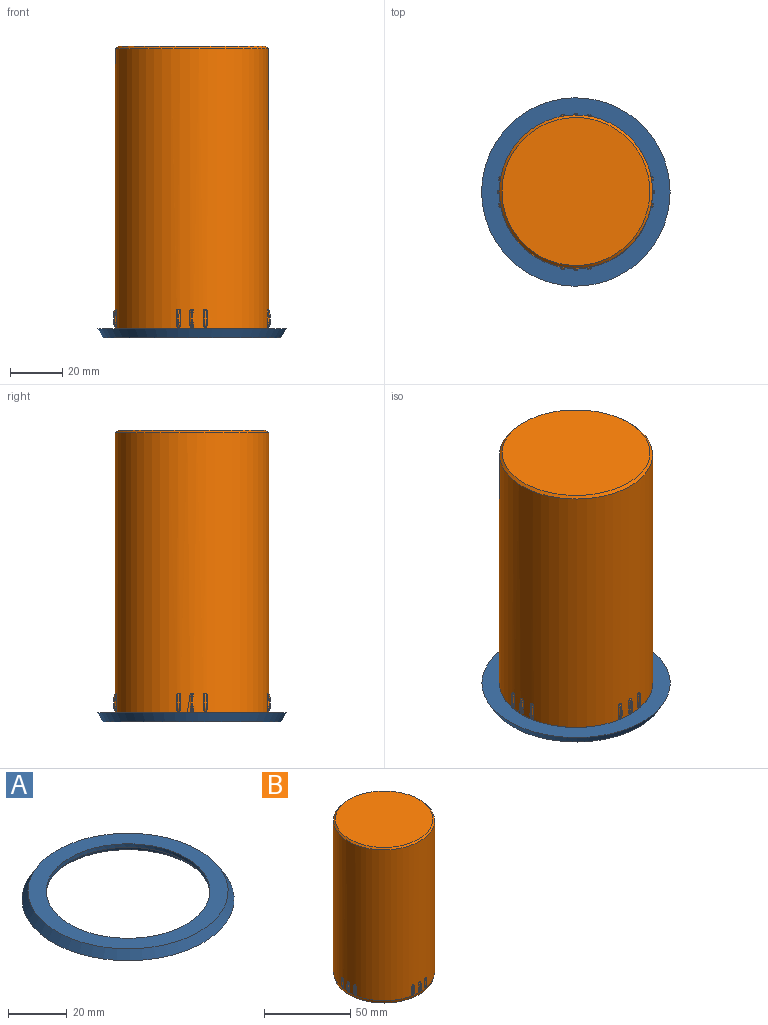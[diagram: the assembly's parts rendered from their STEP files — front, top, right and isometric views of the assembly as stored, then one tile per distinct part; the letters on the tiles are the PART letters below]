
ASSEMBLY  parts=2 mates=1
PART A: 6 faces, bbox 72x72x3.5 mm
  f0: cone r=34mm half-angle=30deg, axis (0,0,-1), area 889mm2, adj f1,f2
  f1: plane 72.04x72.04mm, normal (0,0,-1), area 1379.2mm2, adj f0,f3
  f2: plane 68x68mm, normal (0,0,1), area 1203.7mm2, adj f0,f5
  f3: cone r=29.3mm half-angle=15deg, axis (0,0,-1), area 377.7mm2, adj f1,f4
  f4: plane 57.53x57.53mm, normal (0,0,-1), area 171.3mm2, adj f3,f5
  f5: cylinder r=27.8mm len=55.6mm, axis (0,0,-1), area 262mm2, adj f2,f4
PART B: 212 faces, bbox 60.4x60.4x110 mm
  f0: cylinder r=29.3mm len=107mm, axis (0,0,1), area 19578.2mm2, adj f5,f6,f7,f8,f9,f10,f11,f12
  f1: plane 56.6x56.6mm, normal (0,0,1), area 2516.1mm2, adj f211
  f2: plane 57.53x57.53mm, normal (0,0,-1), area 171.3mm2, adj f3,f209
  f3: cylinder r=27.8mm len=107mm, axis (0,0,1), area 18690mm2, adj f2,f210
  f4: plane 52.6x52.6mm, normal (0,0,-1), area 2173mm2, adj f210
  f5: plane 4.86x0.23mm, normal (0,-1,0), area 0.6mm2, adj f0,f10,f11,f20,f21
  f6: plane 4.86x0.23mm, normal (0,1,0), area 0.6mm2, adj f0,f7,f8,f18,f19
  f7: cylinder r=0.5mm len=1.04mm, axis (0.5,0,0.87), area 0.5mm2, adj f0,f6,f14,f18
  f8: torus R=1.5mm, axis (0,-1,0), area 0.6mm2, adj f0,f6,f9,f17,f19
  f9: cylinder r=0.5mm len=0.61mm, axis (-0.5,0,0.87), area 0.2mm2, adj f0,f8,f13
  f10: cylinder r=0.5mm len=1.04mm, axis (-0.5,0,-0.87), area 0.5mm2, adj f0,f5,f14,f20
  f11: torus R=1.5mm, axis (0,-1,0), area 0.6mm2, adj f0,f5,f12,f17,f21
  f12: cylinder r=0.5mm len=0.61mm, axis (0.5,0,-0.87), area 0.2mm2, adj f0,f11,f13
  f13: plane 0.5x0.45mm, normal (0.87,0,0.5), area 0.3mm2, adj f0,f9,f12,f17
  f14: plane 0.79x0.5mm, normal (0.87,0,-0.5), area 0.5mm2, adj f0,f7,f10,f15
  f15: cylinder r=2mm len=1.1mm, axis (0,1,0), area 0.6mm2, adj f14,f16,f18,f20
  f16: plane 3.72x0.5mm, normal (1,0,0.05), area 1.9mm2, adj f15,f17,f19,f21
  f17: cylinder r=2mm len=0.9mm, axis (0,1,0), area 0.5mm2, adj f8,f11,f13,f16
  f18: torus R=1.5mm, axis (0,-1,0), area 0.8mm2, adj f6,f7,f15,f19
  f19: cylinder r=0.5mm len=3.75mm, axis (-0.05,0,1), area 2.9mm2, adj f6,f8,f16,f18
  f20: torus R=1.5mm, axis (0,-1,0), area 0.8mm2, adj f5,f10,f15,f21
  f21: cylinder r=0.5mm len=3.75mm, axis (0.05,0,-1), area 2.9mm2, adj f5,f11,f16,f20
  f22: plane 4.86x0.23mm, normal (0.17,-0.98,0), area 0.6mm2, adj f0,f27,f28,f37,f38
  f23: plane 4.86x0.23mm, normal (-0.17,0.98,0), area 0.6mm2, adj f0,f24,f25,f35,f36
  f24: cylinder r=0.5mm len=1.04mm, axis (0.49,0.09,0.87), area 0.5mm2, adj f0,f23,f31,f35
  f25: torus R=1.5mm, axis (0.17,-0.98,0), area 0.6mm2, adj f0,f23,f26,f34,f36
  f26: cylinder r=0.5mm len=0.61mm, axis (-0.49,-0.09,0.87), area 0.2mm2, adj f0,f25,f30
  f27: cylinder r=0.5mm len=1.04mm, axis (-0.49,-0.09,-0.87), area 0.5mm2, adj f0,f22,f31,f37
  f28: torus R=1.5mm, axis (0.17,-0.98,0), area 0.6mm2, adj f0,f22,f29,f34,f38
  f29: cylinder r=0.5mm len=0.61mm, axis (0.49,0.09,-0.87), area 0.2mm2, adj f0,f28,f30
  f30: plane 0.54x0.46mm, normal (0.85,0.15,0.5), area 0.3mm2, adj f0,f26,f29,f34
  f31: plane 0.79x0.58mm, normal (0.85,0.15,-0.5), area 0.5mm2, adj f0,f24,f27,f32
  f32: cylinder r=2mm len=1.1mm, axis (-0.17,0.98,0), area 0.6mm2, adj f31,f33,f35,f37
  f33: plane 3.72x0.53mm, normal (0.98,0.17,0.05), area 1.9mm2, adj f32,f34,f36,f38
  f34: cylinder r=2mm len=0.9mm, axis (-0.17,0.98,0), area 0.5mm2, adj f25,f28,f30,f33
  f35: torus R=1.5mm, axis (0.17,-0.98,0), area 0.8mm2, adj f23,f24,f32,f36
  f36: cylinder r=0.5mm len=3.75mm, axis (-0.05,-0.01,1), area 2.9mm2, adj f23,f25,f33,f35
  f37: torus R=1.5mm, axis (0.17,-0.98,0), area 0.8mm2, adj f22,f27,f32,f38
  f38: cylinder r=0.5mm len=3.75mm, axis (0.05,0.01,-1), area 2.9mm2, adj f22,f28,f33,f37
  f39: plane 4.86x0.23mm, normal (0.98,-0.17,0), area 0.6mm2, adj f0,f44,f45,f54,f55
  f40: plane 4.86x0.23mm, normal (-0.98,0.17,0), area 0.6mm2, adj f0,f41,f42,f52,f53
  f41: cylinder r=0.5mm len=1.04mm, axis (0.09,0.49,0.87), area 0.5mm2, adj f0,f40,f48,f52
  f42: torus R=1.5mm, axis (0.98,-0.17,0), area 0.6mm2, adj f0,f40,f43,f51,f53
  f43: cylinder r=0.5mm len=0.61mm, axis (-0.09,-0.49,0.87), area 0.2mm2, adj f0,f42,f47
  f44: cylinder r=0.5mm len=1.04mm, axis (-0.09,-0.49,-0.87), area 0.5mm2, adj f0,f39,f48,f54
  f45: torus R=1.5mm, axis (0.98,-0.17,0), area 0.6mm2, adj f0,f39,f46,f51,f55
  f46: cylinder r=0.5mm len=0.61mm, axis (0.09,0.49,-0.87), area 0.2mm2, adj f0,f45,f47
  f47: plane 0.54x0.46mm, normal (0.15,0.85,0.5), area 0.3mm2, adj f0,f43,f46,f51
  f48: plane 0.79x0.58mm, normal (0.15,0.85,-0.5), area 0.5mm2, adj f0,f41,f44,f49
  f49: cylinder r=2mm len=1.1mm, axis (-0.98,0.17,0), area 0.6mm2, adj f48,f50,f52,f54
  f50: plane 3.72x0.53mm, normal (0.17,0.98,0.05), area 1.9mm2, adj f49,f51,f53,f55
  f51: cylinder r=2mm len=0.9mm, axis (-0.98,0.17,0), area 0.5mm2, adj f42,f45,f47,f50
  f52: torus R=1.5mm, axis (0.98,-0.17,0), area 0.8mm2, adj f40,f41,f49,f53
  f53: cylinder r=0.5mm len=3.75mm, axis (-0.01,-0.05,1), area 2.9mm2, adj f40,f42,f50,f52
  f54: torus R=1.5mm, axis (0.98,-0.17,0), area 0.8mm2, adj f39,f44,f49,f55
  f55: cylinder r=0.5mm len=3.75mm, axis (0.01,0.05,-1), area 2.9mm2, adj f39,f45,f50,f54
  f56: plane 4.86x0.23mm, normal (1,0,0), area 0.6mm2, adj f0,f61,f62,f71,f72
  f57: plane 4.86x0.23mm, normal (-1,0,0), area 0.6mm2, adj f0,f58,f59,f69,f70
  f58: cylinder r=0.5mm len=1.04mm, axis (0,0.5,0.87), area 0.5mm2, adj f0,f57,f65,f69
  f59: torus R=1.5mm, axis (1,0,0), area 0.6mm2, adj f0,f57,f60,f68,f70
  f60: cylinder r=0.5mm len=0.61mm, axis (0,-0.5,0.87), area 0.2mm2, adj f0,f59,f64
  f61: cylinder r=0.5mm len=1.04mm, axis (0,-0.5,-0.87), area 0.5mm2, adj f0,f56,f65,f71
  f62: torus R=1.5mm, axis (1,0,0), area 0.6mm2, adj f0,f56,f63,f68,f72
  f63: cylinder r=0.5mm len=0.61mm, axis (0,0.5,-0.87), area 0.2mm2, adj f0,f62,f64
  f64: plane 0.5x0.46mm, normal (0,0.87,0.5), area 0.3mm2, adj f0,f60,f63,f68
  f65: plane 0.79x0.5mm, normal (0,0.87,-0.5), area 0.5mm2, adj f0,f58,f61,f66
  f66: cylinder r=2mm len=1.1mm, axis (-1,0,0), area 0.6mm2, adj f65,f67,f69,f71
  f67: plane 3.72x0.5mm, normal (0,1,0.05), area 1.9mm2, adj f66,f68,f70,f72
  f68: cylinder r=2mm len=0.9mm, axis (-1,0,0), area 0.5mm2, adj f59,f62,f64,f67
  f69: torus R=1.5mm, axis (1,0,0), area 0.8mm2, adj f57,f58,f66,f70
  f70: cylinder r=0.5mm len=3.75mm, axis (0,-0.05,1), area 2.9mm2, adj f57,f59,f67,f69
  f71: torus R=1.5mm, axis (1,0,0), area 0.8mm2, adj f56,f61,f66,f72
  f72: cylinder r=0.5mm len=3.75mm, axis (0,0.05,-1), area 2.9mm2, adj f56,f62,f67,f71
  f73: plane 4.86x0.23mm, normal (0.98,0.17,0), area 0.6mm2, adj f0,f78,f79,f88,f89
  f74: plane 4.86x0.23mm, normal (-0.98,-0.17,0), area 0.6mm2, adj f0,f75,f76,f86,f87
  f75: cylinder r=0.5mm len=1.04mm, axis (-0.09,0.49,0.87), area 0.5mm2, adj f0,f74,f82,f86
  f76: torus R=1.5mm, axis (0.98,0.17,0), area 0.6mm2, adj f0,f74,f77,f85,f87
  f77: cylinder r=0.5mm len=0.61mm, axis (0.09,-0.49,0.87), area 0.2mm2, adj f0,f76,f81
  f78: cylinder r=0.5mm len=1.04mm, axis (0.09,-0.49,-0.87), area 0.5mm2, adj f0,f73,f82,f88
  f79: torus R=1.5mm, axis (0.98,0.17,0), area 0.6mm2, adj f0,f73,f80,f85,f89
  f80: cylinder r=0.5mm len=0.61mm, axis (-0.09,0.49,-0.87), area 0.2mm2, adj f0,f79,f81
  f81: plane 0.54x0.46mm, normal (-0.15,0.85,0.5), area 0.3mm2, adj f0,f77,f80,f85
  f82: plane 0.79x0.58mm, normal (-0.15,0.85,-0.5), area 0.5mm2, adj f0,f75,f78,f83
  f83: cylinder r=2mm len=1.1mm, axis (-0.98,-0.17,0), area 0.6mm2, adj f82,f84,f86,f88
  f84: plane 3.72x0.53mm, normal (-0.17,0.98,0.05), area 1.9mm2, adj f83,f85,f87,f89
  f85: cylinder r=2mm len=0.9mm, axis (-0.98,-0.17,0), area 0.5mm2, adj f76,f79,f81,f84
  f86: torus R=1.5mm, axis (0.98,0.17,0), area 0.8mm2, adj f74,f75,f83,f87
  f87: cylinder r=0.5mm len=3.75mm, axis (0.01,-0.05,1), area 2.9mm2, adj f74,f76,f84,f86
  f88: torus R=1.5mm, axis (0.98,0.17,0), area 0.8mm2, adj f73,f78,f83,f89
  f89: cylinder r=0.5mm len=3.75mm, axis (-0.01,0.05,-1), area 2.9mm2, adj f73,f79,f84,f88
  f90: plane 4.86x0.23mm, normal (0.17,0.98,0), area 0.6mm2, adj f0,f95,f96,f105,f106
  f91: plane 4.86x0.23mm, normal (-0.17,-0.98,0), area 0.6mm2, adj f0,f92,f93,f103,f104
  f92: cylinder r=0.5mm len=1.04mm, axis (-0.49,0.09,0.87), area 0.5mm2, adj f0,f91,f99,f103
  f93: torus R=1.5mm, axis (0.17,0.98,0), area 0.6mm2, adj f0,f91,f94,f102,f104
  f94: cylinder r=0.5mm len=0.61mm, axis (0.49,-0.09,0.87), area 0.2mm2, adj f0,f93,f98
  f95: cylinder r=0.5mm len=1.04mm, axis (0.49,-0.09,-0.87), area 0.5mm2, adj f0,f90,f99,f105
  f96: torus R=1.5mm, axis (0.17,0.98,0), area 0.6mm2, adj f0,f90,f97,f102,f106
  f97: cylinder r=0.5mm len=0.61mm, axis (-0.49,0.09,-0.87), area 0.2mm2, adj f0,f96,f98
  f98: plane 0.54x0.46mm, normal (-0.85,0.15,0.5), area 0.3mm2, adj f0,f94,f97,f102
  f99: plane 0.79x0.58mm, normal (-0.85,0.15,-0.5), area 0.5mm2, adj f0,f92,f95,f100
  f100: cylinder r=2mm len=1.1mm, axis (-0.17,-0.98,0), area 0.6mm2, adj f99,f101,f103,f105
  f101: plane 3.72x0.53mm, normal (-0.98,0.17,0.05), area 1.9mm2, adj f100,f102,f104,f106
  f102: cylinder r=2mm len=0.9mm, axis (-0.17,-0.98,0), area 0.5mm2, adj f93,f96,f98,f101
  f103: torus R=1.5mm, axis (0.17,0.98,0), area 0.8mm2, adj f91,f92,f100,f104
  f104: cylinder r=0.5mm len=3.75mm, axis (0.05,-0.01,1), area 2.9mm2, adj f91,f93,f101,f103
  f105: torus R=1.5mm, axis (0.17,0.98,0), area 0.8mm2, adj f90,f95,f100,f106
  f106: cylinder r=0.5mm len=3.75mm, axis (-0.05,0.01,-1), area 2.9mm2, adj f90,f96,f101,f105
  f107: plane 4.86x0.23mm, normal (0,1,0), area 0.6mm2, adj f0,f112,f113,f122,f123
  f108: plane 4.86x0.23mm, normal (0,-1,0), area 0.6mm2, adj f0,f109,f110,f120,f121
  f109: cylinder r=0.5mm len=1.04mm, axis (-0.5,0,0.87), area 0.5mm2, adj f0,f108,f116,f120
  f110: torus R=1.5mm, axis (0,1,0), area 0.6mm2, adj f0,f108,f111,f119,f121
  f111: cylinder r=0.5mm len=0.61mm, axis (0.5,0,0.87), area 0.2mm2, adj f0,f110,f115
  f112: cylinder r=0.5mm len=1.04mm, axis (0.5,0,-0.87), area 0.5mm2, adj f0,f107,f116,f122
  f113: torus R=1.5mm, axis (0,1,0), area 0.6mm2, adj f0,f107,f114,f119,f123
  f114: cylinder r=0.5mm len=0.61mm, axis (-0.5,0,-0.87), area 0.2mm2, adj f0,f113,f115
  f115: plane 0.5x0.46mm, normal (-0.87,0,0.5), area 0.3mm2, adj f0,f111,f114,f119
  f116: plane 0.79x0.5mm, normal (-0.87,0,-0.5), area 0.5mm2, adj f0,f109,f112,f117
  f117: cylinder r=2mm len=1.1mm, axis (0,-1,0), area 0.6mm2, adj f116,f118,f120,f122
  f118: plane 3.72x0.5mm, normal (-1,0,0.05), area 1.9mm2, adj f117,f119,f121,f123
  f119: cylinder r=2mm len=0.9mm, axis (0,-1,0), area 0.5mm2, adj f110,f113,f115,f118
  f120: torus R=1.5mm, axis (0,1,0), area 0.8mm2, adj f108,f109,f117,f121
  f121: cylinder r=0.5mm len=3.75mm, axis (0.05,0,1), area 2.9mm2, adj f108,f110,f118,f120
  f122: torus R=1.5mm, axis (0,1,0), area 0.8mm2, adj f107,f112,f117,f123
  f123: cylinder r=0.5mm len=3.75mm, axis (-0.05,0,-1), area 2.9mm2, adj f107,f113,f118,f122
  f124: plane 4.86x0.23mm, normal (-0.17,0.98,0), area 0.6mm2, adj f0,f129,f130,f139,f140
  f125: plane 4.86x0.23mm, normal (0.17,-0.98,0), area 0.6mm2, adj f0,f126,f127,f137,f138
  f126: cylinder r=0.5mm len=1.04mm, axis (-0.49,-0.09,0.87), area 0.5mm2, adj f0,f125,f133,f137
  f127: torus R=1.5mm, axis (-0.17,0.98,0), area 0.6mm2, adj f0,f125,f128,f136,f138
  f128: cylinder r=0.5mm len=0.61mm, axis (0.49,0.09,0.87), area 0.2mm2, adj f0,f127,f132
  f129: cylinder r=0.5mm len=1.04mm, axis (0.49,0.09,-0.87), area 0.5mm2, adj f0,f124,f133,f139
  f130: torus R=1.5mm, axis (-0.17,0.98,0), area 0.6mm2, adj f0,f124,f131,f136,f140
  f131: cylinder r=0.5mm len=0.61mm, axis (-0.49,-0.09,-0.87), area 0.2mm2, adj f0,f130,f132
  f132: plane 0.54x0.46mm, normal (-0.85,-0.15,0.5), area 0.3mm2, adj f0,f128,f131,f136
  f133: plane 0.79x0.58mm, normal (-0.85,-0.15,-0.5), area 0.5mm2, adj f0,f126,f129,f134
  f134: cylinder r=2mm len=1.1mm, axis (0.17,-0.98,0), area 0.6mm2, adj f133,f135,f137,f139
  f135: plane 3.72x0.53mm, normal (-0.98,-0.17,0.05), area 1.9mm2, adj f134,f136,f138,f140
  f136: cylinder r=2mm len=0.9mm, axis (0.17,-0.98,0), area 0.5mm2, adj f127,f130,f132,f135
  f137: torus R=1.5mm, axis (-0.17,0.98,0), area 0.8mm2, adj f125,f126,f134,f138
  f138: cylinder r=0.5mm len=3.75mm, axis (0.05,0.01,1), area 2.9mm2, adj f125,f127,f135,f137
  f139: torus R=1.5mm, axis (-0.17,0.98,0), area 0.8mm2, adj f124,f129,f134,f140
  f140: cylinder r=0.5mm len=3.75mm, axis (-0.05,-0.01,-1), area 2.9mm2, adj f124,f130,f135,f139
  f141: plane 4.86x0.23mm, normal (-0.98,0.17,0), area 0.6mm2, adj f0,f146,f147,f156,f157
  f142: plane 4.86x0.23mm, normal (0.98,-0.17,0), area 0.6mm2, adj f0,f143,f144,f154,f155
  f143: cylinder r=0.5mm len=1.04mm, axis (-0.09,-0.49,0.87), area 0.5mm2, adj f0,f142,f150,f154
  f144: torus R=1.5mm, axis (-0.98,0.17,0), area 0.6mm2, adj f0,f142,f145,f153,f155
  f145: cylinder r=0.5mm len=0.61mm, axis (0.09,0.49,0.87), area 0.2mm2, adj f0,f144,f149
  f146: cylinder r=0.5mm len=1.04mm, axis (0.09,0.49,-0.87), area 0.5mm2, adj f0,f141,f150,f156
  f147: torus R=1.5mm, axis (-0.98,0.17,0), area 0.6mm2, adj f0,f141,f148,f153,f157
  f148: cylinder r=0.5mm len=0.61mm, axis (-0.09,-0.49,-0.87), area 0.2mm2, adj f0,f147,f149
  f149: plane 0.54x0.46mm, normal (-0.15,-0.85,0.5), area 0.3mm2, adj f0,f145,f148,f153
  f150: plane 0.79x0.58mm, normal (-0.15,-0.85,-0.5), area 0.5mm2, adj f0,f143,f146,f151
  f151: cylinder r=2mm len=1.1mm, axis (0.98,-0.17,0), area 0.6mm2, adj f150,f152,f154,f156
  f152: plane 3.72x0.53mm, normal (-0.17,-0.98,0.05), area 1.9mm2, adj f151,f153,f155,f157
  f153: cylinder r=2mm len=0.9mm, axis (0.98,-0.17,0), area 0.5mm2, adj f144,f147,f149,f152
  f154: torus R=1.5mm, axis (-0.98,0.17,0), area 0.8mm2, adj f142,f143,f151,f155
  f155: cylinder r=0.5mm len=3.75mm, axis (0.01,0.05,1), area 2.9mm2, adj f142,f144,f152,f154
  f156: torus R=1.5mm, axis (-0.98,0.17,0), area 0.8mm2, adj f141,f146,f151,f157
  f157: cylinder r=0.5mm len=3.75mm, axis (-0.01,-0.05,-1), area 2.9mm2, adj f141,f147,f152,f156
  f158: plane 4.86x0.23mm, normal (-1,0,0), area 0.6mm2, adj f0,f163,f164,f173,f174
  f159: plane 4.86x0.23mm, normal (1,0,0), area 0.6mm2, adj f0,f160,f161,f171,f172
  f160: cylinder r=0.5mm len=1.04mm, axis (0,-0.5,0.87), area 0.5mm2, adj f0,f159,f167,f171
  f161: torus R=1.5mm, axis (-1,0,0), area 0.6mm2, adj f0,f159,f162,f170,f172
  f162: cylinder r=0.5mm len=0.61mm, axis (0,0.5,0.87), area 0.2mm2, adj f0,f161,f166
  f163: cylinder r=0.5mm len=1.04mm, axis (0,0.5,-0.87), area 0.5mm2, adj f0,f158,f167,f173
  f164: torus R=1.5mm, axis (-1,0,0), area 0.6mm2, adj f0,f158,f165,f170,f174
  f165: cylinder r=0.5mm len=0.61mm, axis (0,-0.5,-0.87), area 0.2mm2, adj f0,f164,f166
  f166: plane 0.5x0.46mm, normal (0,-0.87,0.5), area 0.3mm2, adj f0,f162,f165,f170
  f167: plane 0.79x0.5mm, normal (0,-0.87,-0.5), area 0.5mm2, adj f0,f160,f163,f168
  f168: cylinder r=2mm len=1.1mm, axis (1,0,0), area 0.6mm2, adj f167,f169,f171,f173
  f169: plane 3.72x0.5mm, normal (0,-1,0.05), area 1.9mm2, adj f168,f170,f172,f174
  f170: cylinder r=2mm len=0.9mm, axis (1,0,0), area 0.5mm2, adj f161,f164,f166,f169
  f171: torus R=1.5mm, axis (-1,0,0), area 0.8mm2, adj f159,f160,f168,f172
  f172: cylinder r=0.5mm len=3.75mm, axis (0,0.05,1), area 2.9mm2, adj f159,f161,f169,f171
  f173: torus R=1.5mm, axis (-1,0,0), area 0.8mm2, adj f158,f163,f168,f174
  f174: cylinder r=0.5mm len=3.75mm, axis (0,-0.05,-1), area 2.9mm2, adj f158,f164,f169,f173
  f175: plane 4.86x0.23mm, normal (-0.98,-0.17,0), area 0.6mm2, adj f0,f180,f181,f190,f191
  f176: plane 4.86x0.23mm, normal (0.98,0.17,0), area 0.6mm2, adj f0,f177,f178,f188,f189
  f177: cylinder r=0.5mm len=1.04mm, axis (0.09,-0.49,0.87), area 0.5mm2, adj f0,f176,f184,f188
  f178: torus R=1.5mm, axis (-0.98,-0.17,0), area 0.6mm2, adj f0,f176,f179,f187,f189
  f179: cylinder r=0.5mm len=0.61mm, axis (-0.09,0.49,0.87), area 0.2mm2, adj f0,f178,f183
  f180: cylinder r=0.5mm len=1.04mm, axis (-0.09,0.49,-0.87), area 0.5mm2, adj f0,f175,f184,f190
  f181: torus R=1.5mm, axis (-0.98,-0.17,0), area 0.6mm2, adj f0,f175,f182,f187,f191
  f182: cylinder r=0.5mm len=0.61mm, axis (0.09,-0.49,-0.87), area 0.2mm2, adj f0,f181,f183
  f183: plane 0.54x0.46mm, normal (0.15,-0.85,0.5), area 0.3mm2, adj f0,f179,f182,f187
  f184: plane 0.79x0.58mm, normal (0.15,-0.85,-0.5), area 0.5mm2, adj f0,f177,f180,f185
  f185: cylinder r=2mm len=1.1mm, axis (0.98,0.17,0), area 0.6mm2, adj f184,f186,f188,f190
  f186: plane 3.72x0.53mm, normal (0.17,-0.98,0.05), area 1.9mm2, adj f185,f187,f189,f191
  f187: cylinder r=2mm len=0.9mm, axis (0.98,0.17,0), area 0.5mm2, adj f178,f181,f183,f186
  f188: torus R=1.5mm, axis (-0.98,-0.17,0), area 0.8mm2, adj f176,f177,f185,f189
  f189: cylinder r=0.5mm len=3.75mm, axis (-0.01,0.05,1), area 2.9mm2, adj f176,f178,f186,f188
  f190: torus R=1.5mm, axis (-0.98,-0.17,0), area 0.8mm2, adj f175,f180,f185,f191
  f191: cylinder r=0.5mm len=3.75mm, axis (0.01,-0.05,-1), area 2.9mm2, adj f175,f181,f186,f190
  f192: plane 4.86x0.23mm, normal (-0.17,-0.98,0), area 0.6mm2, adj f0,f197,f198,f207,f208
  f193: plane 4.86x0.23mm, normal (0.17,0.98,0), area 0.6mm2, adj f0,f194,f195,f205,f206
  f194: cylinder r=0.5mm len=1.04mm, axis (0.49,-0.09,0.87), area 0.5mm2, adj f0,f193,f201,f205
  f195: torus R=1.5mm, axis (-0.17,-0.98,0), area 0.6mm2, adj f0,f193,f196,f204,f206
  f196: cylinder r=0.5mm len=0.61mm, axis (-0.49,0.09,0.87), area 0.2mm2, adj f0,f195,f200
  f197: cylinder r=0.5mm len=1.04mm, axis (-0.49,0.09,-0.87), area 0.5mm2, adj f0,f192,f201,f207
  f198: torus R=1.5mm, axis (-0.17,-0.98,0), area 0.6mm2, adj f0,f192,f199,f204,f208
  f199: cylinder r=0.5mm len=0.61mm, axis (0.49,-0.09,-0.87), area 0.2mm2, adj f0,f198,f200
  f200: plane 0.54x0.46mm, normal (0.85,-0.15,0.5), area 0.3mm2, adj f0,f196,f199,f204
  f201: plane 0.79x0.58mm, normal (0.85,-0.15,-0.5), area 0.5mm2, adj f0,f194,f197,f202
  f202: cylinder r=2mm len=1.1mm, axis (0.17,0.98,0), area 0.6mm2, adj f201,f203,f205,f207
  f203: plane 3.72x0.53mm, normal (0.98,-0.17,0.05), area 1.9mm2, adj f202,f204,f206,f208
  f204: cylinder r=2mm len=0.9mm, axis (0.17,0.98,0), area 0.5mm2, adj f195,f198,f200,f203
  f205: torus R=1.5mm, axis (-0.17,-0.98,0), area 0.8mm2, adj f193,f194,f202,f206
  f206: cylinder r=0.5mm len=3.75mm, axis (-0.05,0.01,1), area 2.9mm2, adj f193,f195,f203,f205
  f207: torus R=1.5mm, axis (-0.17,-0.98,0), area 0.8mm2, adj f192,f197,f202,f208
  f208: cylinder r=0.5mm len=3.75mm, axis (0.05,-0.01,-1), area 2.9mm2, adj f192,f198,f203,f207
  f209: cone r=29.3mm half-angle=15deg, axis (0,0,1), area 377.7mm2, adj f0,f2
  f210: torus R=26.3mm, axis (0,0,1), area 403.5mm2, adj f3,f4
  f211: cone r=28.3mm half-angle=45deg, axis (0,0,-1), area 255.9mm2, adj f0,f1
PLACE A rot(axis=(1,0,0),180deg) t=(0,0,28.71)mm
PLACE B rot(axis=(-1,0,0),0deg) t=(-71.05,0,-79.8)mm
MATE cylindrical B.f0 <-> A.f3  axis (0,0,1) through (-71.05,0,-26.3)mm
